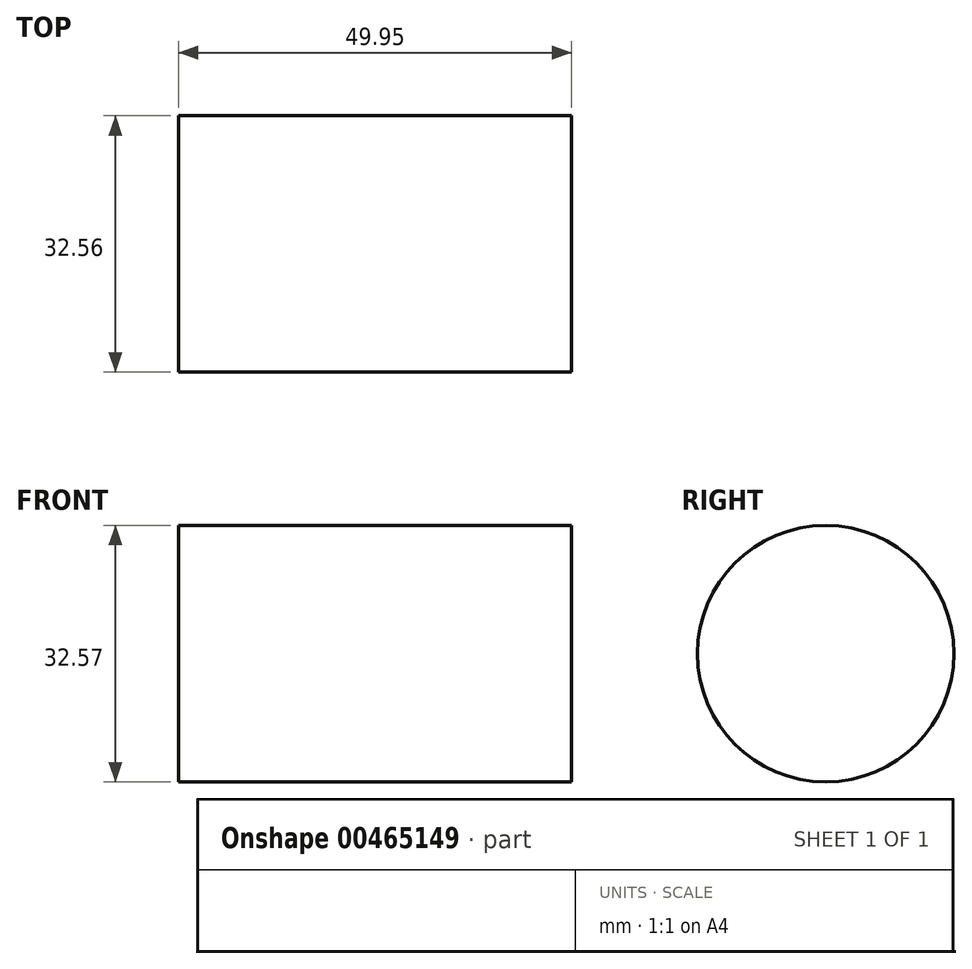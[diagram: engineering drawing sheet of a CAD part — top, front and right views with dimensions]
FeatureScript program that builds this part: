
annotation { "Feature Type Name" : "Feature", "Feature Type Description" : "" }
export const myFeature = defineFeature(function(context is Context, id is Id, definition is map)
    precondition{}
    {
        {
            var Q0;
            Q0=qCreatedBy(makeId("Right.planeOp"),FACE);
            var sketch = newSketch(context, id + "F0", { "sketchPlane" : qUnion([Q0])});
            skCircle(sketch, "E0", {"center": v(0, 19.67) * mm, "radius": 16.28 * mm});
            skSolve(sketch);
        }
        {
            var Q0;
            Q0=sQuery(id+"F0.wireOp",EDGE,"E0");
            extrude(context, id + "F1", {"bodyType" : ToolBodyType.SURFACE, "surfaceEntities" : qUnion([Q0]), "depth" : 49.95 * mm});
        }
    });
